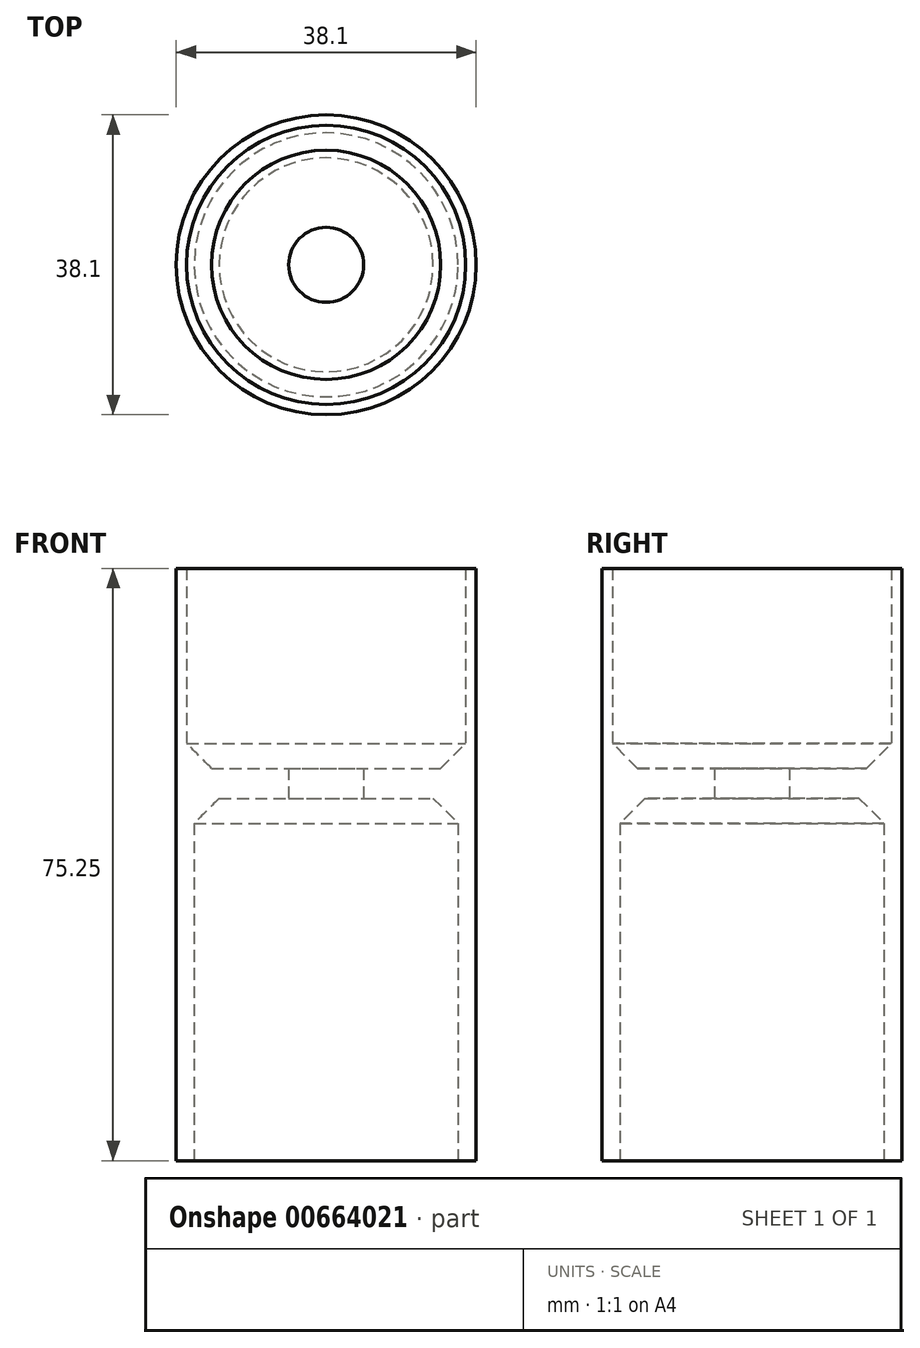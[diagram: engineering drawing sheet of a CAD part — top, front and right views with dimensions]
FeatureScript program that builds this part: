
annotation { "Feature Type Name" : "Feature", "Feature Type Description" : "" }
export const myFeature = defineFeature(function(context is Context, id is Id, definition is map)
    precondition{}
    {
        {
            var Q0;
            Q0=qCreatedBy(makeId("Front.planeOp"),FACE);
            var sketch = newSketch(context, id + "F0", { "sketchPlane" : qUnion([Q0])});
            skLineSegment(sketch, "E0", {"start": v(0, 0) * mm, "end": v(0, 35.16) * mm});
            skLineSegment(sketch, "E1", {"start": v(16.76, 0) * mm, "end": v(19.05, 0) * mm});
            skLineSegment(sketch, "E2", {"start": v(19.05, 0) * mm, "end": v(19.05, 75.25) * mm});
            skLineSegment(sketch, "E3", {"start": v(19.05, 75.25) * mm, "end": v(17.73, 75.25) * mm});
            skLineSegment(sketch, "E4", {"start": v(17.73, 75.25) * mm, "end": v(17.73, 53.02) * mm});
            skLineSegment(sketch, "E5", {"start": v(4.76, 49.85) * mm, "end": v(4.76, 46.04) * mm});
            skLineSegment(sketch, "E6", {"start": v(16.76, 0) * mm, "end": v(16.76, 42.86) * mm});
            skLineSegment(sketch, "E7", {"start": v(4.76, 46.04) * mm, "end": v(13.59, 46.04) * mm});
            skLineSegment(sketch, "E8", {"start": v(13.59, 46.04) * mm, "end": v(16.76, 42.86) * mm});
            skLineSegment(sketch, "E9", {"start": v(4.76, 49.85) * mm, "end": v(14.55, 49.85) * mm});
            skLineSegment(sketch, "E10", {"start": v(14.55, 49.85) * mm, "end": v(17.73, 53.02) * mm});
            skSolve(sketch);
        }
        {
            var Q0;
            Q0=makeQuery(id+"F0.imprint","IMPRINT",FACE,{"disambiguationData":[TD([[makeQuery(id+"F0.imprint","IMPRINT",EDGE,{"derivedFrom":sQuery(id+"F0.wireOp",EDGE,"E1")}),1.0]])]});
            var Q1;
            Q1=sQuery(id+"F0.wireOp",EDGE,"E0");
            revolve(context, id + "F1", {"entities" : qUnion([Q0]), "axis" : qUnion([Q1]), "revolveType" : RevolveType.FULL});
        }
    });
